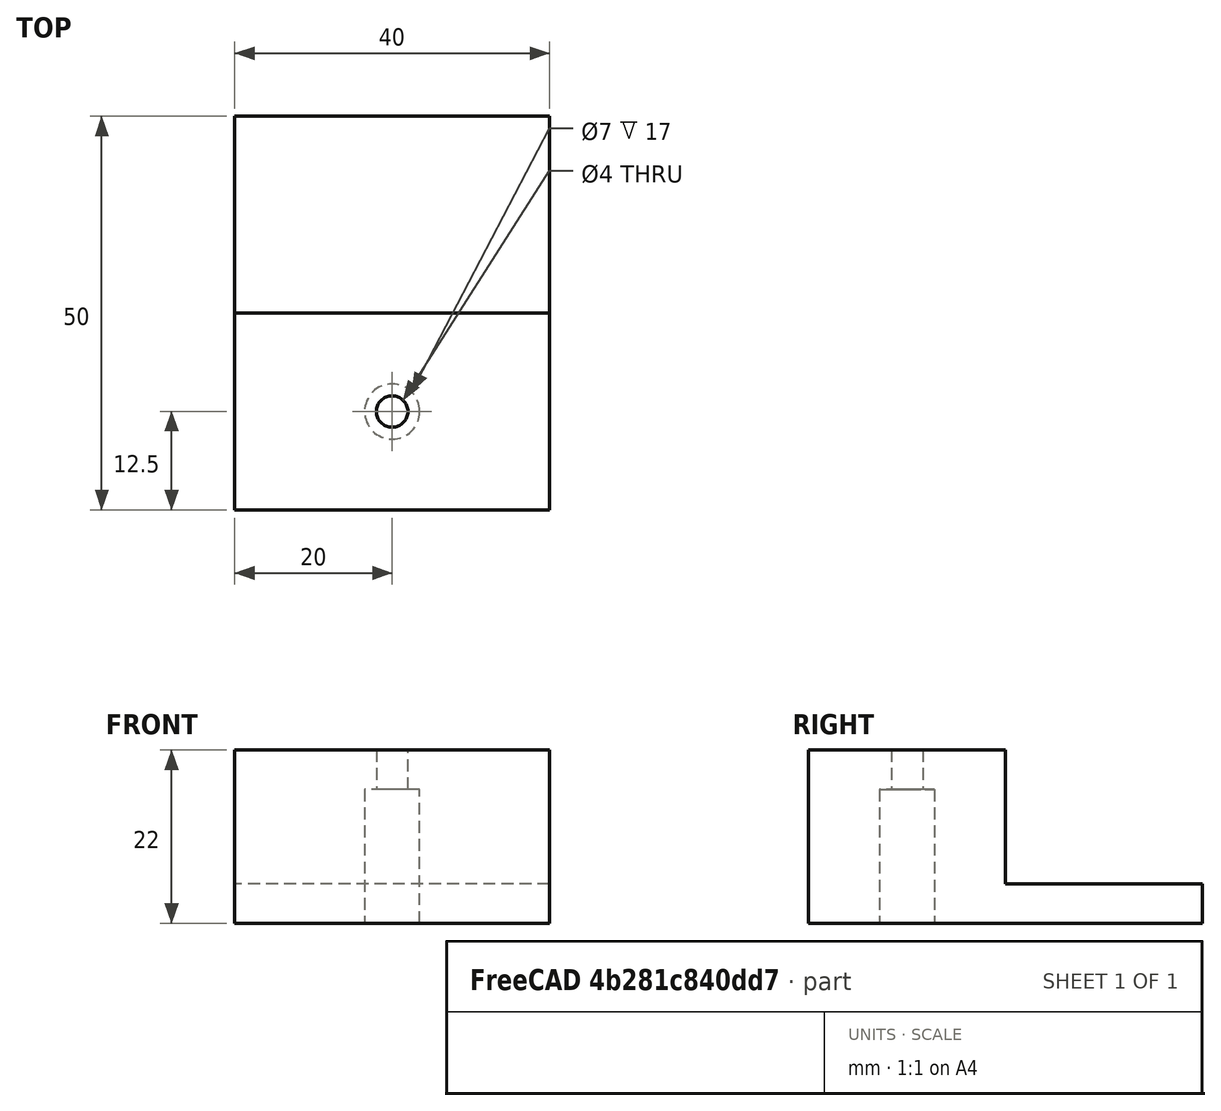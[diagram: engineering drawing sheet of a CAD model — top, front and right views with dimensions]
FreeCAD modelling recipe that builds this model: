
FCSTD DOCUMENT  (FreeCAD 0.20R29603 (Git))
Label: soportes
License: All rights reserved
LicenseURL: http://en.wikipedia.org/wiki/All_rights_reserved
objects: Part::Box×2, Part::Cylinder×2, Part::Cut×2, Part::MultiFuse×1, Mesh::Feature×1
note: 7 computed .brp shape members not serialized (recipe doc carries the construction recipe); baked Part::Feature solids carry a one-line shape summary decoded from their .brp

FEATURE [Part::Box] Box  label="Cube"
  AttacherType = Attacher::AttachEngine3D
  Height = 5
  Length = 40
  Width = 50
FEATURE [Part::Box] Box001  label="Cube001"
  AttacherType = Attacher::AttachEngine3D
  Height = 22
  Length = 40
  Width = 25
FEATURE [Part::Cylinder] Cylinder
  Angle = 360
  AttacherType = Attacher::AttachEngine3D
  FirstAngle = 0
  Height = 31
  Placement = pos=(20,12.5,-5) rot=(0,0,1;0rad)
  Radius = 2
  SecondAngle = 0
FEATURE [Part::Cylinder] Cylinder001
  Angle = 360
  AttacherType = Attacher::AttachEngine3D
  FirstAngle = 0
  Height = 22
  Placement = pos=(20,12.5,-5) rot=(0,0,1;0rad)
  Radius = 3.5
  SecondAngle = 0
FEATURE [Part::MultiFuse] Fusion
  Shapes = -> [Box,Box001]
FEATURE [Part::Cut] Cut
  Base = -> Fusion
  Tool = -> Cylinder
FEATURE [Part::Cut] Cut001  label="tope_trasero"
  Base = -> Cut
  Tool = -> Cylinder001
FEATURE [Mesh::Feature] Mesh  label="tope_trasero001"
